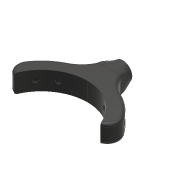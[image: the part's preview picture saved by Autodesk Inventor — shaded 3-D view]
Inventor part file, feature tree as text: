
AUTODESK INVENTOR PART (.ipt)
format: ipt  version: 2017 (Build 210142000, 142)  size: 429,568 bytes
history: native  units: mm
features: sketch x9, extrude x7, plane x7, fillet x4, loft x1, other x1, projected_geometry x1
ambient origin geometry x8: Origin, YZ Plane, XZ Plane, XY Plane, X Axis, Y Axis, Z Axis, Center Point
bodies: Solid1 (feature_tree)
feature tree (30):
  extrude  "Extrusion1"  Depth=35.0mm
  plane  "Work Plane1"
  sketch  "Sketch3"  dims[d3=10.0mm d7=6.981317mm]
  sketch  "Sketch4"  dims[d8=60.0deg d9=7.0mm d11=10.0mm d12=14.0mm]
  plane  "Work Plane2"
  extrude  "Extrusion2"  Depth=6.981317mm
  loft  "Loft1"
  fillet  "Fillet1"  Radius=10.0mm
  fillet  "Fillet2"  Radius=14.0mm
  extrude  "Extrusion3"  [1 undecoded]
  plane  "Work Plane3"
  sketch  "Sketch6"  dims[d16=-5.5mm d17=14.0mm d18=0.0mm]
  plane  "Work Plane4"
  plane  "Work Plane5"
  plane  "Work Plane6"
  plane  "Work Plane7"
  sketch  "Sketch7"  dims[d19=0.0mm d20=90.0deg d21=0.0mm d22=90.0deg]
  sketch  "Sketch8"  dims[d23=2.0mm d24=2.0mm]
  sketch  "Sketch9"  dims[d25=8.2mm d26=22.0mm d27=0.0mm d28=6.981317mm d29=60.0deg]
  sketch  "Sketch10"  dims[d30=120.0deg d31=24.43461mm d32=3.5mm d33=3.5mm d34=3.5mm d35=3.5mm d36=22.0mm d37=0.0mm d38=22.0mm d39=0.0mm d40=22.0mm d41=0.0mm d42=22.0mm d43=0.0mm d44=4.0mm d45=4.0mm]
  extrude  "Extrusion4"  Depth=14.0mm TaperAngle=0.0deg
  extrude  "Extrusion5"  TaperAngle=0.0deg  [1 undecoded]
  extrude  "Extrusion6"  Depth=2.0mm
  extrude  "Extrusion7"  Depth=22.0mm TaperAngle=0.0deg
  fillet  "Fillet3"  Radius=6.981317mm
  fillet  "Fillet4"  [1 undecoded]
  sketch  "Sketch1"  dims[d1=24.43461mm d2=35.0mm]
  other  "Edges1"
  sketch  "Sketch5"  dims[d13=14.0mm d14=0.0mm d15=-11.0mm]
  projected_geometry  "Project Cut Edges2"
note: 3 required parameter values undecoded (feature->parameter linkage not recoverable at this tier; creation-order binding heuristic only, values carry confidence <= 0.55)
